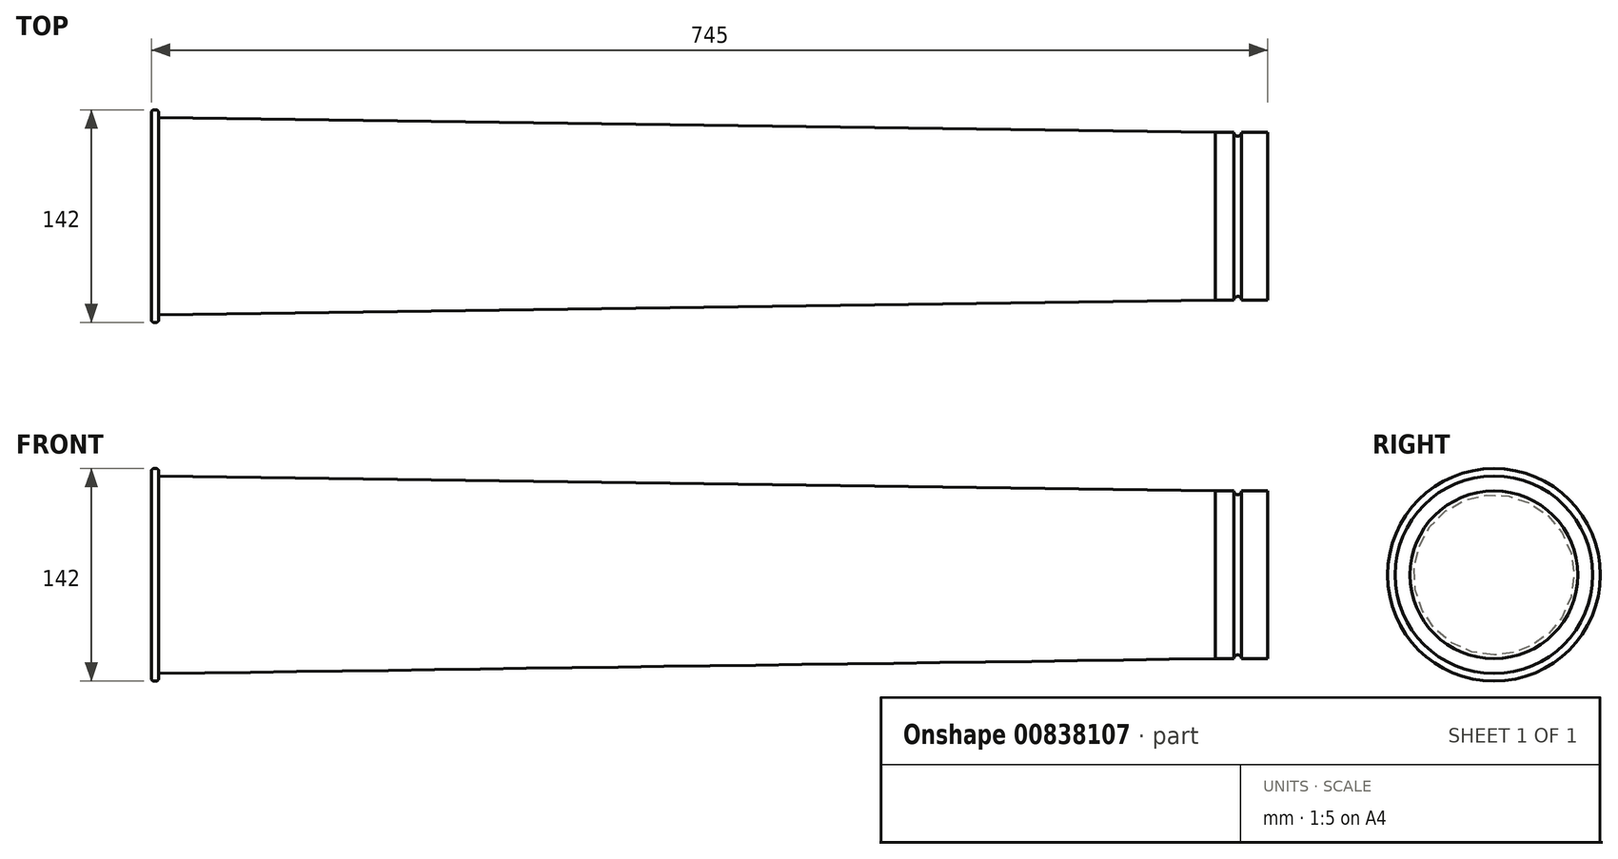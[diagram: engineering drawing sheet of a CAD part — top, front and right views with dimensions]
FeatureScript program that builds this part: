
annotation { "Feature Type Name" : "Feature", "Feature Type Description" : "" }
export const myFeature = defineFeature(function(context is Context, id is Id, definition is map)
    precondition{}
    {
        {
            var Q0;
            Q0=qCreatedBy(makeId("Front.planeOp"),FACE);
            var sketch = newSketch(context, id + "F0", { "sketchPlane" : qUnion([Q0])});
            skLineSegment(sketch, "E0", {"start": v(0, 0) * mm, "end": v(0, 66) * mm});
            skLineSegment(sketch, "E1", {"start": v(0, 66) * mm, "end": v(710, 56) * mm});
            skLineSegment(sketch, "E2", {"start": v(710, 56) * mm, "end": v(710, 0) * mm});
            skLineSegment(sketch, "E3", {"start": v(710, 0) * mm, "end": v(0, 0) * mm});
            skLineSegment(sketch, "E4.bottom", {"start": v(710, 56) * mm, "end": v(745, 56) * mm});
            skLineSegment(sketch, "E4.top", {"start": v(710, 0) * mm, "end": v(745, 0) * mm});
            skLineSegment(sketch, "E4.right", {"start": v(745, 56) * mm, "end": v(745, 0) * mm});
            skPoint(sketch, "E5", {"position": v(725, 56) * mm});
            skCircle(sketch, "E6", {"center": v(725, 56) * mm, "radius": 2.5 * mm});
            skLineSegment(sketch, "E7", {"start": v(0, 66) * mm, "end": v(0, 69) * mm});
            skLineSegment(sketch, "E8", {"start": v(2, 71) * mm, "end": v(3, 71) * mm});
            skLineSegment(sketch, "E9", {"start": v(5, 69) * mm, "end": v(5, 65.93) * mm});
            skPoint(sketch, "E10.visualSharp", {"position": v(0, 71) * mm});
            skArc(sketch, "E10.filletArc", {"start": v(2, 71) * mm, "mid": v(0.59, 70.41) * mm, "end": v(0, 69) * mm});
            skPoint(sketch, "E11.visualSharp", {"position": v(5, 71) * mm});
            skArc(sketch, "E11.filletArc", {"start": v(5, 69) * mm, "mid": v(4.41, 70.41) * mm, "end": v(3, 71) * mm});
            skSolve(sketch);
        }
        {
            var Q0;
            Q0=makeQuery(id+"F0.imprint","IMPRINT",FACE,{"disambiguationData":[TD([[makeQuery(id+"F0.imprint","IMPRINT",EDGE,{"derivedFrom":sQuery(id+"F0.wireOp",EDGE,"E0")}),-1.0]])]});
            var Q1;
            Q1=makeQuery(id+"F0.imprint","IMPRINT",FACE,{"disambiguationData":[TD([[makeQuery(id+"F0.imprint","IMPRINT",EDGE,{"derivedFrom":sQuery(id+"F0.wireOp",EDGE,"E4.top")}),1.0]])]});
            var Q2;
            {var subQ0=sQuery(id+"F0.wireOp",EDGE,"E7");Q2=makeQuery(id+"F0.imprint","IMPRINT",FACE,{"disambiguationData":[TD([[makeQuery(id+"F0.imprint","IMPRINT",EDGE,{"derivedFrom":subQ0}),-1.0]])]});}
            var Q3;
            Q3=sQuery(id+"F0.wireOp",EDGE,"E3");
            revolve(context, id + "F1", {"surfaceOperationType" : NewSurfaceOperationType.NEW, "entities" : qUnion([Q0, Q1, Q2]), "axis" : qUnion([Q3]), "revolveType" : RevolveType.FULL});
        }
    });
